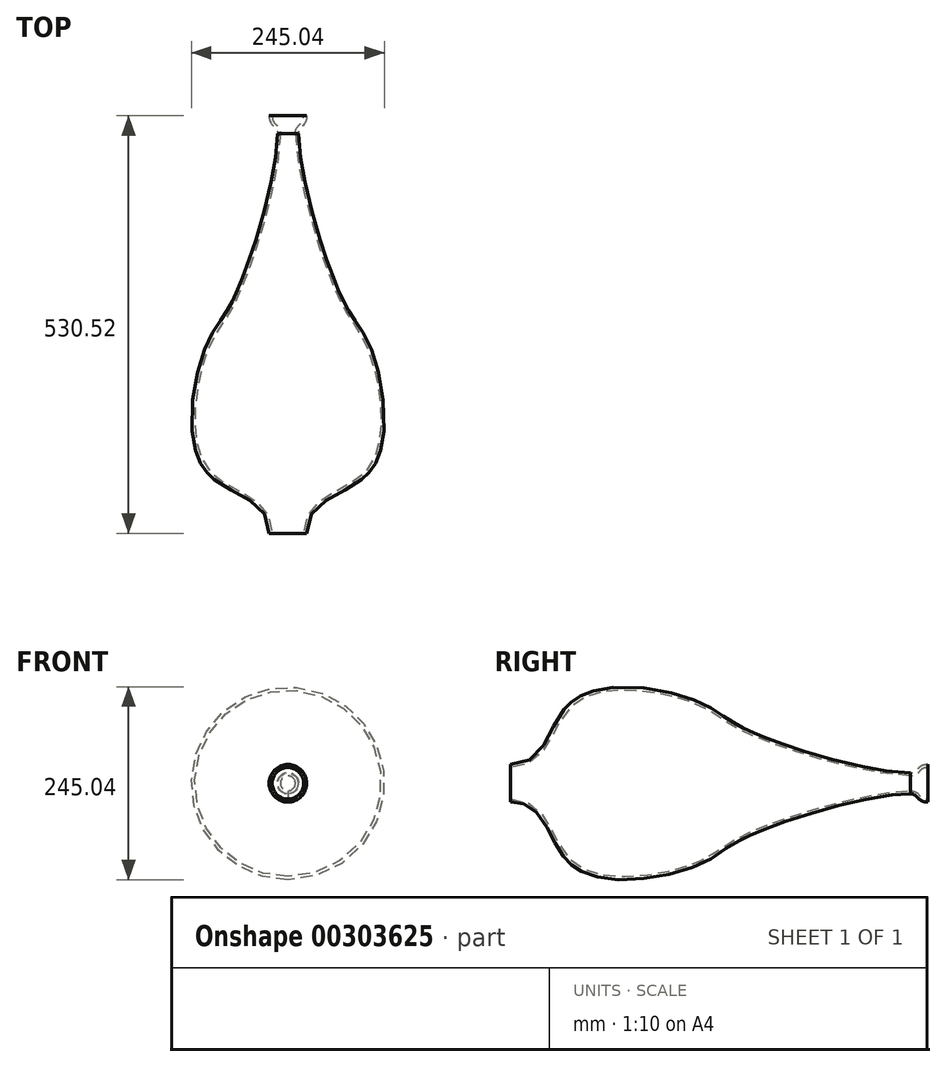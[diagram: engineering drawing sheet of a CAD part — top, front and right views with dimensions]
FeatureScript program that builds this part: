
annotation { "Feature Type Name" : "Feature", "Feature Type Description" : "" }
export const myFeature = defineFeature(function(context is Context, id is Id, definition is map)
    precondition{}
    {
        {
            var Q0;
            Q0=qCreatedBy(makeId("Right.planeOp"),FACE);
            var sketch = newSketch(context, id + "F0", { "sketchPlane" : qUnion([Q0])});
            skLineSegment(sketch, "E0", {"start": v(-254, 0) * mm, "end": v(254, 0) * mm, "construction": true});
            skLineSegment(sketch, "E1", {"start": v(-254, 0) * mm, "end": v(-254, 20) * mm, "construction": true});
            skLineSegment(sketch, "E2", {"start": v(-254, 20) * mm, "end": v(-172.4, 101.6) * mm, "construction": true});
            skLineSegment(sketch, "E3", {"start": v(-172.4, 101.6) * mm, "end": v(-20, 101.6) * mm, "construction": true});
            skLineSegment(sketch, "E4", {"start": v(-20, 101.6) * mm, "end": v(40.38, 66.74) * mm, "construction": true});
            skLineSegment(sketch, "E5", {"start": v(40.38, 66.74) * mm, "end": v(254, 9.5) * mm, "construction": true});
            skLineSegment(sketch, "E6", {"start": v(254, 9.5) * mm, "end": v(254, 0) * mm, "construction": true});
            skFitSpline(sketch, "E7", {"points": [v(-254, 20) * mm, v(-172.4, 101.6) * mm, v(-20, 101.6) * mm, v(40.38, 66.74) * mm, v(254, 9.5) * mm], "startDerivative": vector(656.97, 0) * mm, "endDerivative": vector(474.57, 0) * mm});
            skLineSegment(sketch, "E8", {"start": v(-203.2, 0) * mm, "end": v(-203.2, 20) * mm, "construction": true});
            skLineSegment(sketch, "E9", {"start": v(203.2, 0) * mm, "end": v(203.2, 9.5) * mm, "construction": true});
            skLineSegment(sketch, "E10", {"start": v(254, 0) * mm, "end": v(276.52, 0) * mm, "construction": true});
            skLineSegment(sketch, "E11", {"start": v(276.52, 0) * mm, "end": v(276.52, 20) * mm, "construction": true});
            skLineSegment(sketch, "E12", {"start": v(276.52, 20) * mm, "end": v(254, 9.5) * mm, "construction": true});
            skFitSpline(sketch, "E13", {"points": [v(254, 9.5) * mm, v(276.52, 20) * mm], "startDerivative": vector(38.1, 0) * mm, "endDerivative": vector(38.1, 0) * mm});
            skLineSegment(sketch, "E14", {"start": v(266.7, 0) * mm, "end": v(266.7, 9.5) * mm, "construction": true});
            skLineSegment(sketch, "E15", {"start": v(263.82, 0) * mm, "end": v(263.82, 20) * mm, "construction": true});
            skFitSpline(sketch, "E16.0", {"points": [v(254, 13.3) * mm, v(254.66, 13.3) * mm, v(255.84, 13.38) * mm, v(257.23, 13.63) * mm, v(258.32, 14) * mm, v(259.2, 14.43) * mm, v(260, 14.96) * mm, v(260.78, 15.61) * mm, v(261.59, 16.4) * mm, v(262.46, 17.33) * mm, v(263.43, 18.37) * mm, v(264.56, 19.49) * mm, v(265.9, 20.62) * mm, v(267.48, 21.69) * mm, v(269.35, 22.6) * mm, v(271.47, 23.3) * mm, v(273.84, 23.71) * mm, v(275.6, 23.81) * mm, v(276.52, 23.81) * mm]});
            skFitSpline(sketch, "E16.1", {"points": [v(-254, 23.8) * mm, v(-250.77, 23.8) * mm, v(-244.8, 24.3) * mm, v(-237.16, 26.28) * mm, v(-230.58, 29.35) * mm, v(-224.83, 33.4) * mm, v(-219.71, 38.35) * mm, v(-213.57, 46) * mm, v(-208.2, 54.94) * mm, v(-203.08, 64.56) * mm, v(-199.21, 71.94) * mm, v(-195.17, 79.32) * mm, v(-190.8, 86.55) * mm, v(-186.72, 92.3) * mm, v(-183.11, 96.65) * mm, v(-180.21, 99.77) * mm, v(-177.62, 102.21) * mm, v(-175.43, 104.07) * mm, v(-173.15, 105.86) * mm, v(-170.18, 107.94) * mm, v(-165.15, 110.95) * mm, v(-158.42, 114.16) * mm, v(-149.74, 117.18) * mm, v(-140.54, 119.43) * mm, v(-127.73, 121.51) * mm, v(-110.92, 122.52) * mm, v(-90.21, 121.61) * mm, v(-69.74, 119) * mm, v(-50.27, 115.1) * mm, v(-32.58, 110.28) * mm, v(-17.42, 104.92) * mm, v(-5.52, 99.37) * mm, v(4.26, 93.6) * mm, v(13.02, 87.68) * mm, v(20.45, 82.58) * mm, v(27.13, 78.36) * mm, v(32.66, 75.1) * mm, v(37.84, 72.28) * mm, v(42.4, 69.97) * mm, v(46.07, 68.2) * mm, v(49.95, 66.41) * mm, v(55.41, 63.98) * mm, v(62.74, 60.89) * mm, v(72.23, 57.12) * mm, v(85.71, 52.07) * mm, v(103.87, 45.77) * mm, v(127.03, 38.46) * mm, v(150.85, 31.65) * mm, v(174.61, 25.55) * mm, v(197.6, 20.42) * mm, v(219.1, 16.46) * mm, v(238.37, 13.92) * mm, v(249.22, 13.3) * mm, v(254, 13.3) * mm]});
            skLineSegment(sketch, "E17", {"start": v(-254, 23.8) * mm, "end": v(-254, 20) * mm});
            skLineSegment(sketch, "E18", {"start": v(276.52, 23.81) * mm, "end": v(276.52, 20) * mm});
            skSolve(sketch);
        }
        {
            var Q0;
            Q0=makeQuery(id+"F0.imprint","IMPRINT",FACE,{"disambiguationData":[TD([[makeQuery(id+"F0.imprint","IMPRINT",EDGE,{"derivedFrom":sQuery(id+"F0.wireOp",EDGE,"E7")}),1.0]])]});
            var Q1;
            Q1=sQuery(id+"F0.wireOp",EDGE,"E0");
            revolve(context, id + "F1", {"entities" : qUnion([Q0]), "axis" : qUnion([Q1]), "revolveType" : RevolveType.FULL});
        }
        {
            var Q0;
            Q0=makeQuery(id+"F1.opRevolve","SWEPT_BODY",BODY,{"disambiguationData":[OSD([sQuery(id+"F0.wireOp",EDGE,"E7"),sQuery(id+"F0.wireOp",EDGE,"E13"),sQuery(id+"F0.wireOp",EDGE,"E16.0"),sQuery(id+"F0.wireOp",EDGE,"E16.1"),sQuery(id+"F0.wireOp",EDGE,"E17"),sQuery(id+"F0.wireOp",EDGE,"E18")])]});
            transform(context, id + "F2", {"entities" : qUnion([Q0]), "transformType" : TransformType.TRANSLATION_3D, "dx" : 0 * mm, "dy" : 0 * mm, "dz" : 0 * mm, "makeCopy" : true});
        }
    });
